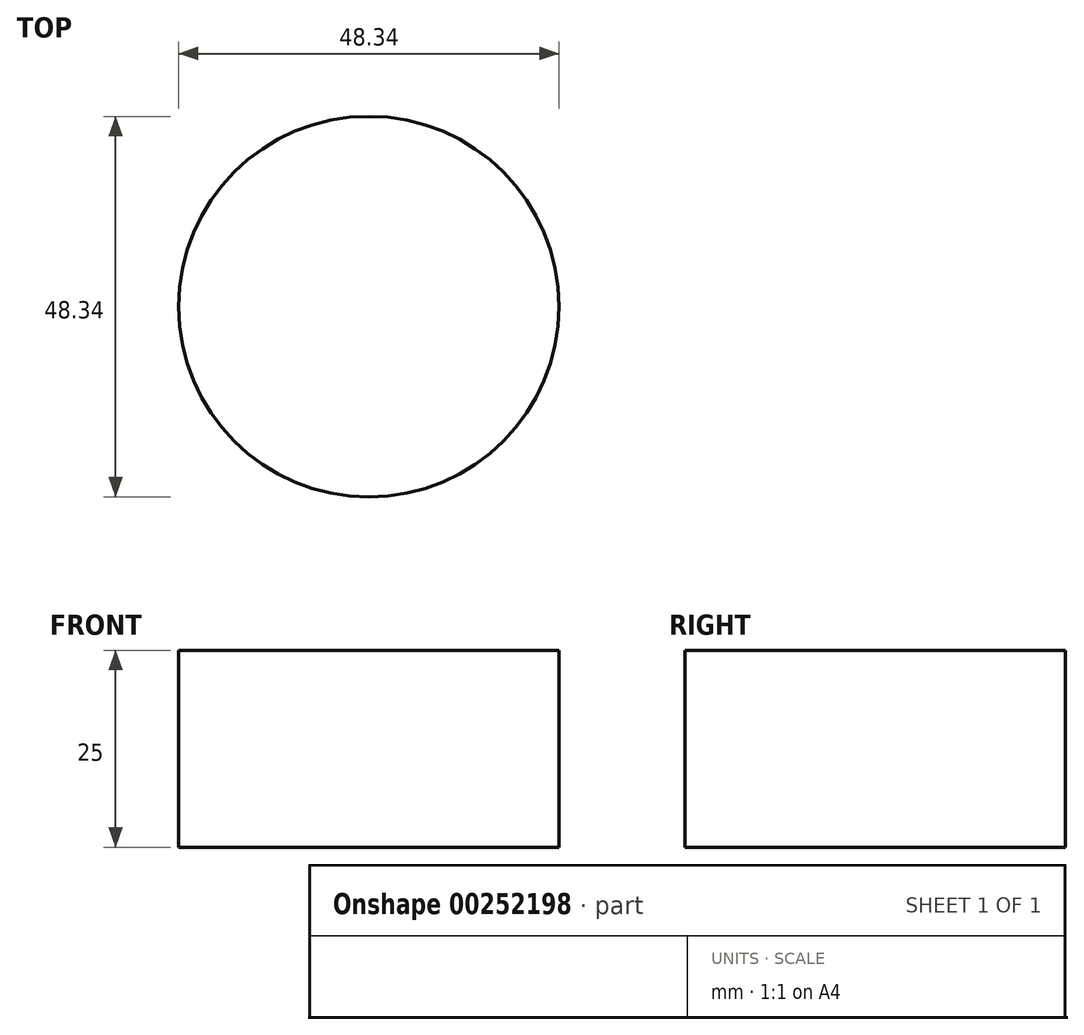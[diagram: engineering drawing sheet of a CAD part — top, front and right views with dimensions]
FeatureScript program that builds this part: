
annotation { "Feature Type Name" : "Feature", "Feature Type Description" : "" }
export const myFeature = defineFeature(function(context is Context, id is Id, definition is map)
    precondition{}
    {
        {
            var Q0;
            Q0=qCreatedBy(makeId("Top.planeOp"),FACE);
            var sketch = newSketch(context, id + "F0", { "sketchPlane" : qUnion([Q0])});
            skCircle(sketch, "E0", {"center": v(-18.83, -35.68) * mm, "radius": 24.17 * mm});
            skSolve(sketch);
        }
        {
            var Q0;
            Q0=makeQuery(id+"F0.imprint","IMPRINT",FACE,{"disambiguationData":[TD([[makeQuery(id+"F0.imprint","IMPRINT",EDGE,{"derivedFrom":sQuery(id+"F0.wireOp",EDGE,"E0")}),1.0]])]});
            extrude(context, id + "F1", {"entities" : qUnion([Q0]), "depth" : 25 * mm});
        }
    });
